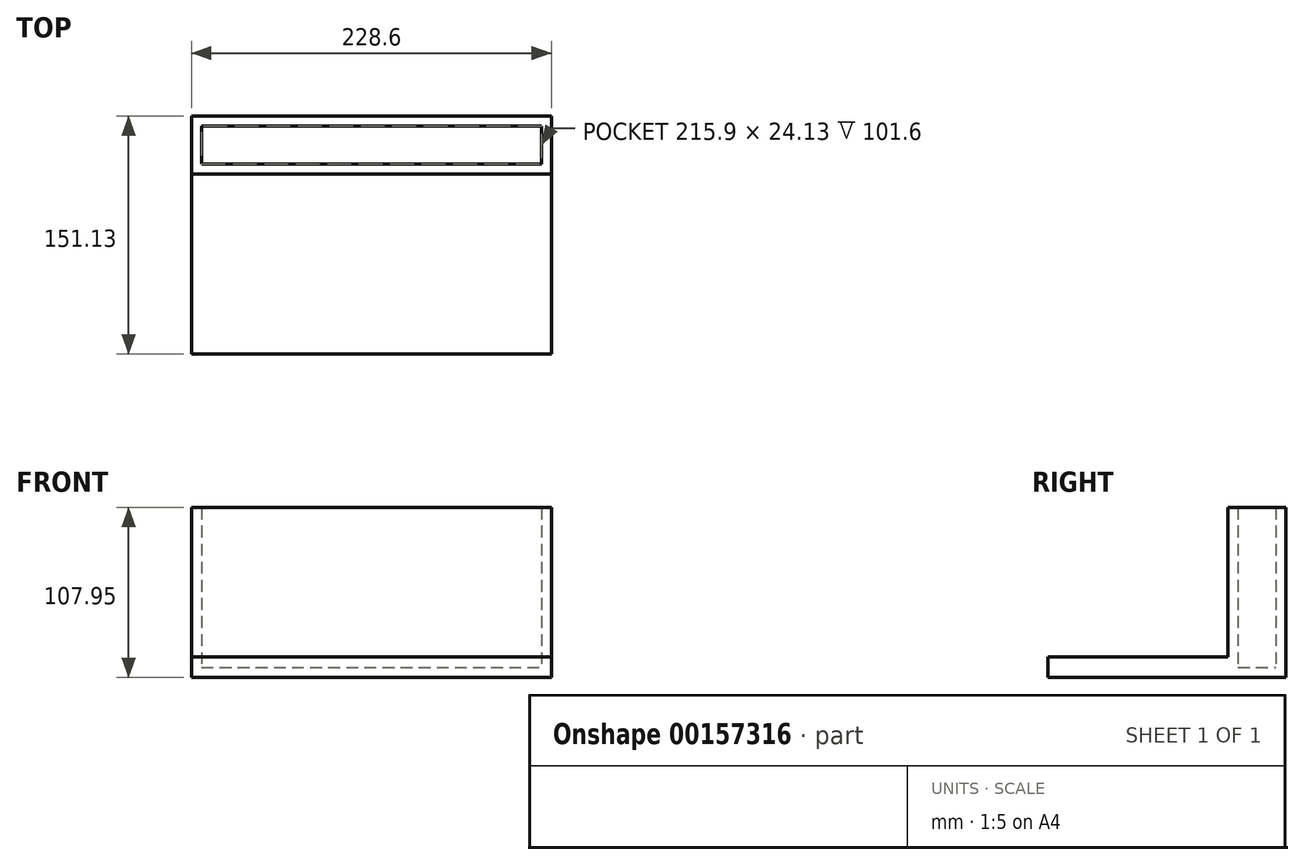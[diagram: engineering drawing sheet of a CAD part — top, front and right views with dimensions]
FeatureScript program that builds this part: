
annotation { "Feature Type Name" : "Feature", "Feature Type Description" : "" }
export const myFeature = defineFeature(function(context is Context, id is Id, definition is map)
    precondition{}
    {
        {
            var Q0;
            Q0=qCreatedBy(makeId("Front.planeOp"),FACE);
            var sketch = newSketch(context, id + "F0", { "sketchPlane" : qUnion([Q0])});
            skLineSegment(sketch, "E0.bottom", {"start": v(-81.63, 49.3) * mm, "end": v(134.27, 49.3) * mm});
            skLineSegment(sketch, "E0.top", {"start": v(-81.63, -52.3) * mm, "end": v(134.27, -52.3) * mm});
            skLineSegment(sketch, "E0.left", {"start": v(-81.63, 49.3) * mm, "end": v(-81.63, -52.3) * mm});
            skLineSegment(sketch, "E0.right", {"start": v(134.27, 49.3) * mm, "end": v(134.27, -52.3) * mm});
            skSolve(sketch);
        }
        {
            var Q0;
            Q0 = qSketchRegion(id + "F0", true);
            extrude(context, id + "F1", {"entities" : qUnion([Q0]), "depth" : 6.35 * mm});
        }
        {
            var Q0;
            Q0=makeQuery(id+"F1.opExtrude","SWEPT_FACE",FACE,{"disambiguationData":[OSD([sQuery(id+"F0.wireOp",EDGE,"E0.left")])]});
            var sketch = newSketch(context, id + "F2", { "sketchPlane" : qUnion([Q0])});
            skLineSegment(sketch, "E1.bottom", {"start": v(6.35, 49.3) * mm, "end": v(-24.13, 49.3) * mm});
            skLineSegment(sketch, "E1.top", {"start": v(6.35, -52.3) * mm, "end": v(-24.13, -52.3) * mm});
            skLineSegment(sketch, "E1.left", {"start": v(6.35, 49.3) * mm, "end": v(6.35, -52.3) * mm});
            skLineSegment(sketch, "E1.right", {"start": v(-24.13, 49.3) * mm, "end": v(-24.13, -52.3) * mm});
            skSolve(sketch);
        }
        {
            var Q0;
            Q0 = qSketchRegion(id + "F2", true);
            extrude(context, id + "F3", {"entities" : qUnion([Q0]), "operationType" : NewBodyOperationType.ADD, "depth" : 6.35 * mm});
        }
        {
            var Q0;
            Q0=makeQuery(id+"F1.opExtrude","SWEPT_FACE",FACE,{"disambiguationData":[OSD([sQuery(id+"F0.wireOp",EDGE,"E0.right")])]});
            var sketch = newSketch(context, id + "F4", { "sketchPlane" : qUnion([Q0])});
            skPoint(sketch, "E2.oppositeSnap0", {"position": v(-3.18, -52.3) * mm});
            skLineSegment(sketch, "E2.bottom", {"start": v(-6.35, 49.3) * mm, "end": v(24.13, 49.3) * mm});
            skLineSegment(sketch, "E2.top", {"start": v(-6.35, -52.3) * mm, "end": v(24.13, -52.3) * mm});
            skLineSegment(sketch, "E2.left", {"start": v(-6.35, 49.3) * mm, "end": v(-6.35, -52.3) * mm});
            skLineSegment(sketch, "E2.right", {"start": v(24.13, 49.3) * mm, "end": v(24.13, -52.3) * mm});
            skSolve(sketch);
        }
        {
            var Q0;
            Q0 = qSketchRegion(id + "F4", true);
            extrude(context, id + "F5", {"entities" : qUnion([Q0]), "operationType" : NewBodyOperationType.ADD, "depth" : 6.35 * mm});
        }
        {
            var Q0;
            Q0=makeQuery(id+"F5.opExtrude","SWEPT_FACE",FACE,{"disambiguationData":[OSD([sQuery(id+"F4.wireOp",EDGE,"E2.right")])]});
            var sketch = newSketch(context, id + "F6", { "sketchPlane" : qUnion([Q0])});
            skPoint(sketch, "E3.oppositeSnap0", {"position": v(-137.45, -52.3) * mm});
            skLineSegment(sketch, "E3.bottom", {"start": v(-140.62, 49.3) * mm, "end": v(87.98, 49.3) * mm});
            skLineSegment(sketch, "E3.top", {"start": v(-140.62, -52.3) * mm, "end": v(87.98, -52.3) * mm});
            skLineSegment(sketch, "E3.left", {"start": v(-140.62, 49.3) * mm, "end": v(-140.62, -52.3) * mm});
            skLineSegment(sketch, "E3.right", {"start": v(87.98, 49.3) * mm, "end": v(87.98, -52.3) * mm});
            skSolve(sketch);
        }
        {
            var Q0;
            Q0 = qSketchRegion(id + "F6", true);
            extrude(context, id + "F7", {"entities" : qUnion([Q0]), "operationType" : NewBodyOperationType.ADD, "depth" : 6.35 * mm});
        }
        {
            var Q0;
            Q0=makeQuery(id+"F7.boolean.opBoolean","MERGE",FACE,{"derivedFrom":[makeQuery(id+"F5.boolean.opBoolean","MERGE",FACE,{"derivedFrom":[makeQuery(id+"F3.boolean.opBoolean","MERGE",FACE,{"derivedFrom":[makeQuery(id+"F1.opExtrude","SWEPT_FACE",FACE,{"disambiguationData":[OSD([sQuery(id+"F0.wireOp",EDGE,"E0.top")])]}),makeQuery(id+"F3.opExtrude","SWEPT_FACE",FACE,{"disambiguationData":[OSD([sQuery(id+"F2.wireOp",EDGE,"E1.top")])]})]}),makeQuery(id+"F5.opExtrude","SWEPT_FACE",FACE,{"disambiguationData":[OSD([sQuery(id+"F4.wireOp",EDGE,"E2.top")])]})]}),makeQuery(id+"F7.opExtrude","SWEPT_FACE",FACE,{"disambiguationData":[OSD([sQuery(id+"F6.wireOp",EDGE,"E3.top")])]})]});
            var sketch = newSketch(context, id + "F8", { "sketchPlane" : qUnion([Q0])});
            skLineSegment(sketch, "E4.bottom", {"start": v(140.62, -30.48) * mm, "end": v(-87.98, -30.48) * mm});
            skLineSegment(sketch, "E4.top", {"start": v(140.62, 6.35) * mm, "end": v(-87.98, 6.35) * mm});
            skLineSegment(sketch, "E4.left", {"start": v(140.62, -30.48) * mm, "end": v(140.62, 6.35) * mm});
            skLineSegment(sketch, "E4.right", {"start": v(-87.98, -30.48) * mm, "end": v(-87.98, 6.35) * mm});
            skSolve(sketch);
        }
        {
            var Q0;
            Q0 = qSketchRegion(id + "F8", true);
            extrude(context, id + "F9", {"entities" : qUnion([Q0]), "operationType" : NewBodyOperationType.ADD, "depth" : 6.35 * mm});
        }
        {
            var Q0;
            Q0=makeQuery(id+"F9.boolean.opBoolean","MERGE",FACE,{"derivedFrom":[makeQuery(id+"F5.boolean.opBoolean","MERGE",FACE,{"derivedFrom":[makeQuery(id+"F3.boolean.opBoolean","MERGE",FACE,{"derivedFrom":[makeQuery(id+"F1.opExtrude","CAP_FACE",FACE,{"disambiguationData":[OSD([sQuery(id+"F0.wireOp",EDGE,"E0.bottom"),sQuery(id+"F0.wireOp",EDGE,"E0.top"),sQuery(id+"F0.wireOp",EDGE,"E0.left"),sQuery(id+"F0.wireOp",EDGE,"E0.right")])],"isStart":false}),makeQuery(id+"F3.opExtrude","SWEPT_FACE",FACE,{"disambiguationData":[OSD([sQuery(id+"F2.wireOp",EDGE,"E1.left")])]})]}),makeQuery(id+"F5.opExtrude","SWEPT_FACE",FACE,{"disambiguationData":[OSD([sQuery(id+"F4.wireOp",EDGE,"E2.left")])]})]}),makeQuery(id+"F9.opExtrude","SWEPT_FACE",FACE,{"disambiguationData":[OSD([sQuery(id+"F8.wireOp",EDGE,"E4.top")])]})]});
            var sketch = newSketch(context, id + "F10", { "sketchPlane" : qUnion([Q0])});
            skLineSegment(sketch, "E5.bottom", {"start": v(140.62, -58.65) * mm, "end": v(-87.98, -58.65) * mm});
            skLineSegment(sketch, "E5.top", {"start": v(140.62, -45.6) * mm, "end": v(-87.98, -45.6) * mm});
            skLineSegment(sketch, "E5.left", {"start": v(140.62, -58.65) * mm, "end": v(140.62, -45.6) * mm});
            skLineSegment(sketch, "E5.right", {"start": v(-87.98, -58.65) * mm, "end": v(-87.98, -45.6) * mm});
            skSolve(sketch);
        }
        {
            var Q0;
            Q0 = qSketchRegion(id + "F10", true);
            extrude(context, id + "F11", {"entities" : qUnion([Q0]), "operationType" : NewBodyOperationType.ADD, "depth" : 114.3 * mm});
        }
    });
